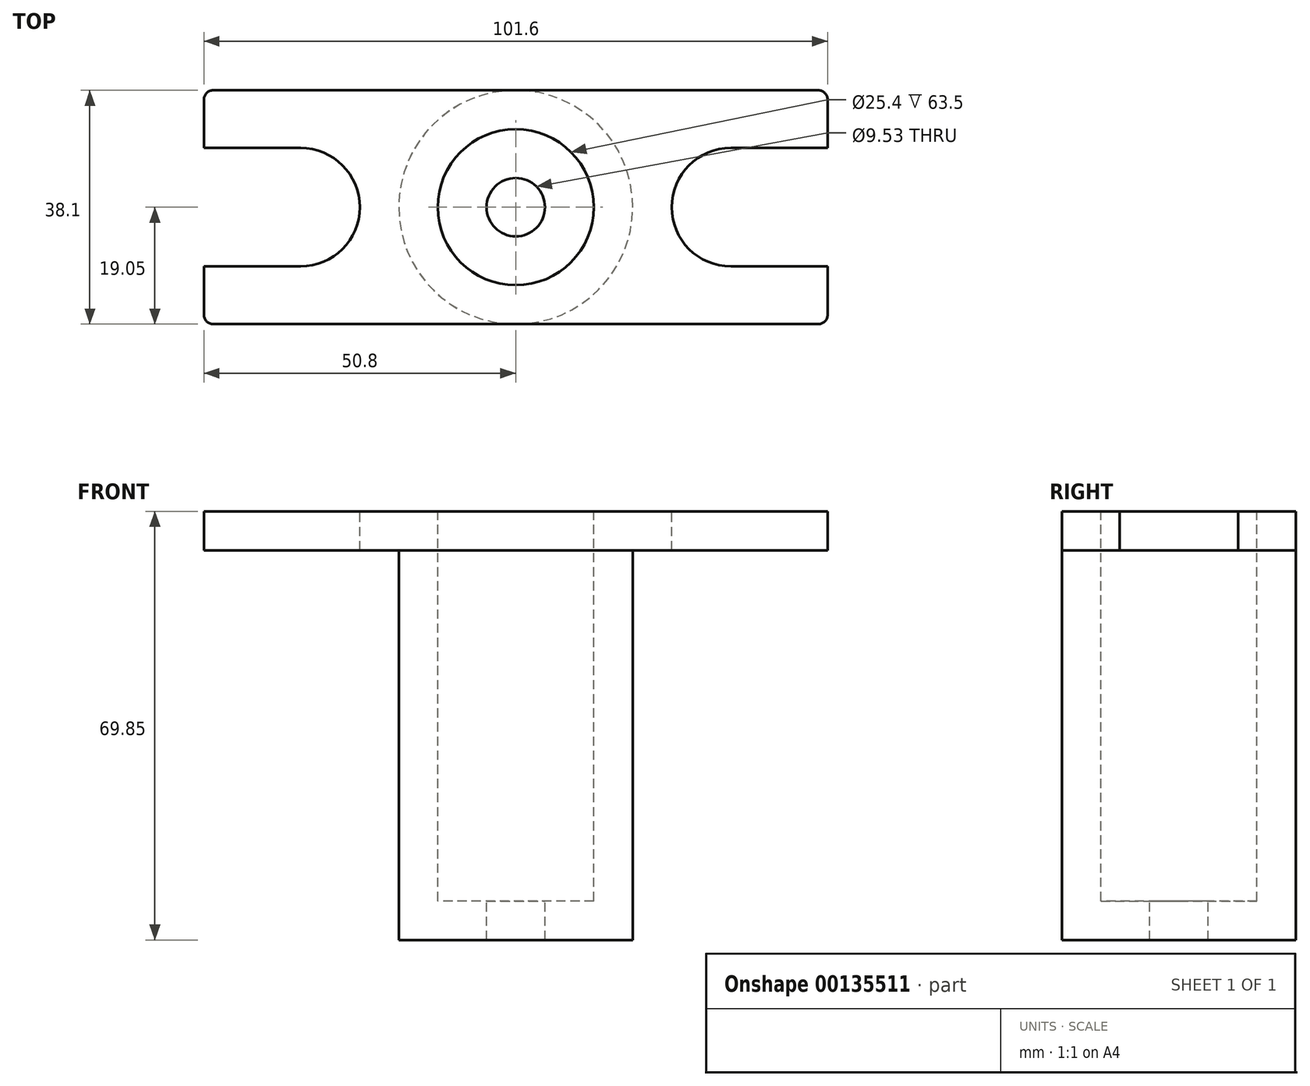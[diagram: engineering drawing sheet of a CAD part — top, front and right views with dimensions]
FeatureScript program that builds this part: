
annotation { "Feature Type Name" : "Feature", "Feature Type Description" : "" }
export const myFeature = defineFeature(function(context is Context, id is Id, definition is map)
    precondition{}
    {
        {
            var Q0;
            Q0=qCreatedBy(makeId("Top.planeOp"),FACE);
            var sketch = newSketch(context, id + "F0", { "sketchPlane" : qUnion([Q0])});
            skLineSegment(sketch, "E0.bottom", {"start": v(-50.8, -19.05) * mm, "end": v(50.8, -19.05) * mm});
            skLineSegment(sketch, "E0.top", {"start": v(-50.8, 19.05) * mm, "end": v(50.8, 19.05) * mm});
            skLineSegment(sketch, "E0.left", {"start": v(-50.8, -19.05) * mm, "end": v(-50.8, -9.65) * mm});
            skLineSegment(sketch, "E0.right", {"start": v(50.8, -19.05) * mm, "end": v(50.8, -9.65) * mm});
            skPoint(sketch, "E0.middle", {"position": v(0, 0) * mm});
            skLineSegment(sketch, "E1", {"start": v(-50.8, 9.65) * mm, "end": v(-35.05, 9.65) * mm});
            skLineSegment(sketch, "E2", {"start": v(-50.8, -9.65) * mm, "end": v(-35.05, -9.65) * mm});
            skLineSegment(sketch, "E3", {"start": v(50.8, 9.65) * mm, "end": v(35.05, 9.65) * mm});
            skLineSegment(sketch, "E4", {"start": v(50.8, -9.65) * mm, "end": v(35.05, -9.65) * mm});
            skArc(sketch, "E5", {"start": v(-35.05, -9.65) * mm, "mid": v(-25.4, 0) * mm, "end": v(-35.05, 9.65) * mm});
            skArc(sketch, "E6", {"start": v(35.05, 9.65) * mm, "mid": v(25.4, 0) * mm, "end": v(35.05, -9.65) * mm});
            skCircle(sketch, "E7", {"center": v(0, 0) * mm, "radius": 12.7 * mm});
            skLineSegment(sketch, "E8.trimOffspring", {"start": v(-50.8, 9.65) * mm, "end": v(-50.8, 19.05) * mm});
            skLineSegment(sketch, "E9.trimOffspring", {"start": v(50.8, 9.65) * mm, "end": v(50.8, 19.05) * mm});
            skSolve(sketch);
        }
        {
            var Q0;
            Q0 = qSketchRegion(id + "F0", true);
            extrude(context, id + "F1", {"entities" : qUnion([Q0]), "oppositeDirection" : true, "depth" : 6.35 * mm});
        }
        {
            var Q0;
            Q0=makeQuery(id+"F1.opExtrude","CAP_FACE",FACE,{"disambiguationData":[OSD([sQuery(id+"F0.wireOp",EDGE,"E0.bottom"),sQuery(id+"F0.wireOp",EDGE,"E0.top"),sQuery(id+"F0.wireOp",EDGE,"E0.left"),sQuery(id+"F0.wireOp",EDGE,"E0.right"),sQuery(id+"F0.wireOp",EDGE,"E1"),sQuery(id+"F0.wireOp",EDGE,"E2"),sQuery(id+"F0.wireOp",EDGE,"E3"),sQuery(id+"F0.wireOp",EDGE,"E4"),sQuery(id+"F0.wireOp",EDGE,"E5"),sQuery(id+"F0.wireOp",EDGE,"E6"),sQuery(id+"F0.wireOp",EDGE,"E7"),sQuery(id+"F0.wireOp",EDGE,"E8.trimOffspring"),sQuery(id+"F0.wireOp",EDGE,"E9.trimOffspring")])],"isStart":false});
            var sketch = newSketch(context, id + "F2", { "sketchPlane" : qUnion([Q0])});
            skCircle(sketch, "E10.0", {"center": v(0, 0) * mm, "radius": 12.7 * mm});
            skCircle(sketch, "E11", {"center": v(0, 0) * mm, "radius": 19.05 * mm});
            skSolve(sketch);
        }
        {
            var Q0;
            Q0 = qSketchRegion(id + "F2", true);
            extrude(context, id + "F3", {"entities" : qUnion([Q0]), "operationType" : NewBodyOperationType.ADD, "depth" : 57.15 * mm});
        }
        {
            var Q0;
            Q0=makeQuery(id+"F3.opExtrude","CAP_FACE",FACE,{"disambiguationData":[OSD([sQuery(id+"F2.wireOp",EDGE,"E10.0"),sQuery(id+"F2.wireOp",EDGE,"E11")])],"isStart":false});
            var sketch = newSketch(context, id + "F4", { "sketchPlane" : qUnion([Q0])});
            skCircle(sketch, "E12.0", {"center": v(0, 0) * mm, "radius": 19.05 * mm});
            skCircle(sketch, "E13", {"center": v(0, 0) * mm, "radius": 4.76 * mm});
            skSolve(sketch);
        }
        {
            var Q0;
            Q0 = qSketchRegion(id + "F4", true);
            extrude(context, id + "F5", {"entities" : qUnion([Q0]), "operationType" : NewBodyOperationType.ADD, "depth" : 6.35 * mm});
        }
        {
            var Q0;
            Q0=makeQuery(id+"F1.opExtrude","SWEPT_EDGE",EDGE,{"disambiguationData":[OSD([sQuery(id+"F0.wireOp",EDGE,"E0.bottom"),sQuery(id+"F0.wireOp",EDGE,"E0.left")])]});
            var Q1;
            Q1=makeQuery(id+"F1.opExtrude","SWEPT_EDGE",EDGE,{"disambiguationData":[OSD([sQuery(id+"F0.wireOp",EDGE,"E0.bottom"),sQuery(id+"F0.wireOp",EDGE,"E0.right")])]});
            var Q2;
            Q2=makeQuery(id+"F1.opExtrude","SWEPT_EDGE",EDGE,{"disambiguationData":[OSD([sQuery(id+"F0.wireOp",EDGE,"E0.top"),sQuery(id+"F0.wireOp",EDGE,"E9.trimOffspring")])]});
            var Q3;
            Q3=makeQuery(id+"F1.opExtrude","SWEPT_EDGE",EDGE,{"disambiguationData":[OSD([sQuery(id+"F0.wireOp",EDGE,"E0.top"),sQuery(id+"F0.wireOp",EDGE,"E8.trimOffspring")])]});
            fillet(context, id + "F6", {"entities" : qUnion([Q0, Q1, Q2, Q3]), "radius" : 1.52 * mm, "tangentPropagation" : true, "allowEdgeOverflow" : false});
        }
    });
